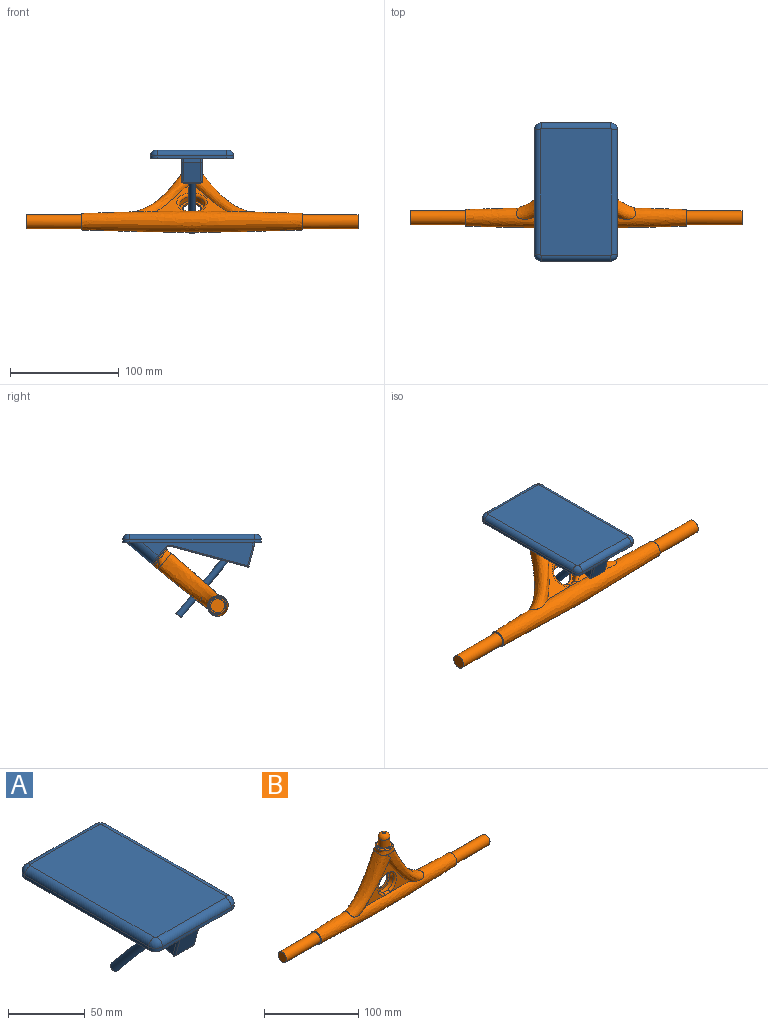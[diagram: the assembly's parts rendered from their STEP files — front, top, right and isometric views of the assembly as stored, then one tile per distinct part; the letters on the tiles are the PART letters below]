
ASSEMBLY  parts=2 mates=1
PART A: 45 faces, bbox 76.2x127x76.8 mm
  f0: plane 16.51x3.2mm, normal (0,0,-1), area 52.8mm2, adj f1,f31,f33,f37
  f1: plane 16.51x15.59mm, normal (0,-0.77,-0.64), area 118.2mm2, adj f0,f2,f3,f27,f28
  f2: cylinder r=1.27mm len=10.53mm, axis (0,-0.64,0.77), area 24.6mm2, adj f1,f24,f28,f37
  f3: cylinder r=1.27mm len=10.53mm, axis (0,0.64,-0.77), area 24.6mm2, adj f1,f22,f28,f33
  f4: plane 114.3x2.54mm, normal (1,0,0), area 290.3mm2, adj f5,f11,f13,f19
  f5: cylinder r=6.35mm len=6.35mm, axis (0,0,-1), area 25.3mm2, adj f4,f6,f13,f21
  f6: plane 63.5x2.54mm, normal (0,1,0), area 161.3mm2, adj f5,f7,f13,f20
  f7: cylinder r=6.35mm len=6.35mm, axis (0,0,-1), area 25.3mm2, adj f6,f8,f13,f18
  f8: plane 114.3x2.54mm, normal (-1,0,0), area 290.3mm2, adj f7,f9,f13,f16
  f9: cylinder r=6.35mm len=6.35mm, axis (0,0,-1), area 25.3mm2, adj f8,f10,f13,f14
  f10: plane 63.5x2.54mm, normal (0,-1,0), area 161.3mm2, adj f9,f11,f13,f15
  f11: cylinder r=6.35mm len=6.35mm, axis (0,0,-1), area 25.3mm2, adj f4,f10,f13,f17
  f12: plane 116.84x66.04mm, normal (0,0,1), area 7714.7mm2, adj f14,f15,f16,f17,f18,f19,f20,f21
  f13: plane 127x76.2mm, normal (0,0,-1), area 7464.4mm2, adj f4,f5,f6,f7,f8,f9,f10,f11
  f14: torus R=1.27mm, axis (0,0,1), area 56.5mm2, adj f9,f12,f15,f16
  f15: cylinder r=5.08mm len=63.5mm, axis (-1,0,0), area 506.7mm2, adj f10,f12,f14,f17
  f16: cylinder r=5.08mm len=114.3mm, axis (0,1,0), area 912.1mm2, adj f8,f12,f14,f18
  f17: torus R=1.27mm, axis (0,0,1), area 56.5mm2, adj f11,f12,f15,f19
  f18: torus R=1.27mm, axis (0,0,1), area 56.5mm2, adj f7,f12,f16,f20
  f19: cylinder r=5.08mm len=114.3mm, axis (0,-1,0), area 912.1mm2, adj f4,f12,f17,f21
  f20: cylinder r=5.08mm len=63.5mm, axis (1,0,0), area 506.7mm2, adj f6,f12,f18,f21
  f21: torus R=1.27mm, axis (0,0,1), area 56.5mm2, adj f5,f12,f19,f20
  f22: plane 101.48x21.3mm, normal (1,0,0), area 1053.9mm2, adj f3,f13,f23,f32,f33,f34,f35
  f23: cylinder r=9.53mm len=29.46mm, axis (0,-0.77,-0.64), area 786.9mm2, adj f13,f22,f24,f28
  f24: plane 101.48x21.3mm, normal (-1,0,0), area 1053.9mm2, adj f2,f13,f23,f37,f39,f40,f42
  f25: cone r=0mm half-angle=59deg, axis (0,-0.77,-0.64), area 153.8mm2, adj f26
  f26: cylinder r=6.48mm len=19.03mm, axis (0,-0.77,-0.64), area 568.5mm2, adj f25,f27
  f27: torus R=7.75mm, axis (0,0.77,0.64), area 87mm2, adj f1,f26
  f28: torus R=8.26mm, axis (0,0.77,0.64), area 56.8mm2, adj f1,f2,f3,f23
  f29: plane 16.51x3.81mm, normal (0,-1,0), area 62.9mm2, adj f13,f30,f32,f40
  f30: plane 17.82x16.51mm, normal (0,-0.97,-0.26), area 304.6mm2, adj f29,f34,f38,f42
  f31: plane 69.87x18.72mm, normal (0,0.26,-0.97), area 1159.3mm2, adj f0,f35,f38,f39,f43
  f32: cylinder r=1.27mm len=3.81mm, axis (0,0,-1), area 7.5mm2, adj f13,f22,f29,f34
  f33: cylinder r=1.27mm len=3.96mm, axis (0,-1,0), area 6.9mm2, adj f0,f3,f22,f35
  f34: cylinder r=1.27mm len=18.15mm, axis (0,0.26,-0.97), area 36.7mm2, adj f22,f30,f32,f36
  f35: cylinder r=1.27mm len=70.36mm, axis (0,0.97,0.26), area 144.4mm2, adj f22,f31,f33,f36
  f36: sphere r=1.27mm, area 2.5mm2, adj f34,f35,f38
  f37: cylinder r=1.27mm len=3.96mm, axis (0,-1,0), area 6.9mm2, adj f0,f2,f24,f39
  f38: cylinder r=1.27mm len=16.51mm, axis (-1,0,0), area 32.9mm2, adj f30,f31,f36,f41
  f39: cylinder r=1.27mm len=70.36mm, axis (0,0.97,0.26), area 144.4mm2, adj f24,f31,f37,f41
  f40: cylinder r=1.27mm len=3.81mm, axis (0,0,-1), area 7.5mm2, adj f13,f24,f29,f42
  f41: sphere r=1.27mm, area 2.5mm2, adj f38,f39,f42
  f42: cylinder r=1.27mm len=18.15mm, axis (0,0.26,-0.97), area 36.7mm2, adj f24,f30,f40,f41
  f43: cylinder r=3.17mm len=55.48mm, axis (0,0.64,-0.77), area 1308.6mm2, adj f31,f44
  f44: plane 6.35x4.86mm, normal (0,0.64,-0.77), area 31.7mm2, adj f43
PART B: 25 faces, bbox 304.9x19.5x94.9 mm
  f0: bspline ~69.45x64.65mm, area 2841.8mm2, adj f3,f8,f9,f10,f11,f18,f19
  f1: plane 15.25x15.25mm, normal (-1,0,0), area 55.7mm2, adj f3,f6
  f2: plane 15.25x15.25mm, normal (1,0,0), area 55.7mm2, adj f3,f4
  f3: bspline ~203.2x19.47mm, area 10039.8mm2, adj f0,f1,f2,f9,f10,f11,f15
  f4: cylinder r=6.35mm len=50.8mm, axis (-1,0,0), area 2026.8mm2, adj f2,f5
  f5: plane 12.7x12.7mm, normal (1,0,0), area 126.7mm2, adj f4
  f6: cylinder r=6.35mm len=50.8mm, axis (1,0,0), area 2026.8mm2, adj f1,f7
  f7: plane 12.7x12.7mm, normal (-1,0,0), area 126.7mm2, adj f6
  f8: bspline ~88.41x67.97mm, area 7.6mm2, adj f0,f19
  f9: bspline ~69.15x64.73mm, area 2855.2mm2, adj f0,f3,f10,f11,f18
  f10: plane 65.78x42.26mm, normal (0,1,0), area 1026mm2, adj f0,f3,f9,f16
  f11: plane 66.52x42.26mm, normal (0,-1,0), area 686.1mm2, adj f0,f3,f9,f14
  f12: cylinder r=11.43mm len=22.86mm, axis (0,-1,0), area 365.3mm2, adj f13,f14,f15
  f13: plane 22.86x22.86mm, normal (0,-1,0), area 162.1mm2, adj f12,f16
  f14: torus R=13.97mm, axis (0,-1,0), area 276mm2, adj f11,f12,f15
  f15: bspline ~10.49x2.75mm, area 28.5mm2, adj f3,f12,f14
  f16: cylinder r=8.89mm len=17.78mm, axis (0,-1,0), area 106.4mm2, adj f10,f13
  f17: plane 16.51x16.2mm, normal (0,0,1), area 83.6mm2, adj f20,f23,f24
  f18: bspline ~19.07x19.06mm, area 258.6mm2, adj f0,f9,f19,f23,f24
  f19: bspline ~16.79x7.84mm, area 65.8mm2, adj f0,f8,f18,f24
  f20: cylinder r=6.35mm len=12.7mm, axis (0,0,-1), area 405.4mm2, adj f17,f22
  f21: plane 2.54x2.54mm, normal (0,0,1), area 5.1mm2, adj f22
  f22: torus R=1.27mm, axis (0,0,1), area 225.8mm2, adj f20,f21
  f23: bspline ~18.86x16.38mm, area 77.3mm2, adj f17,f18,f24
  f24: bspline ~16.23x6.53mm, area 35.7mm2, adj f17,f18,f19,f23
PLACE A t=(-15.79,-18.2,12.05)mm
PLACE B rot(axis=(-1,0,0),50deg) t=(-15.79,-60.83,-46)mm
MATE slider A.f25 <-> B.f20  axis (0,-0.77,-0.64) through (-15.79,7.43,11.28)mm
